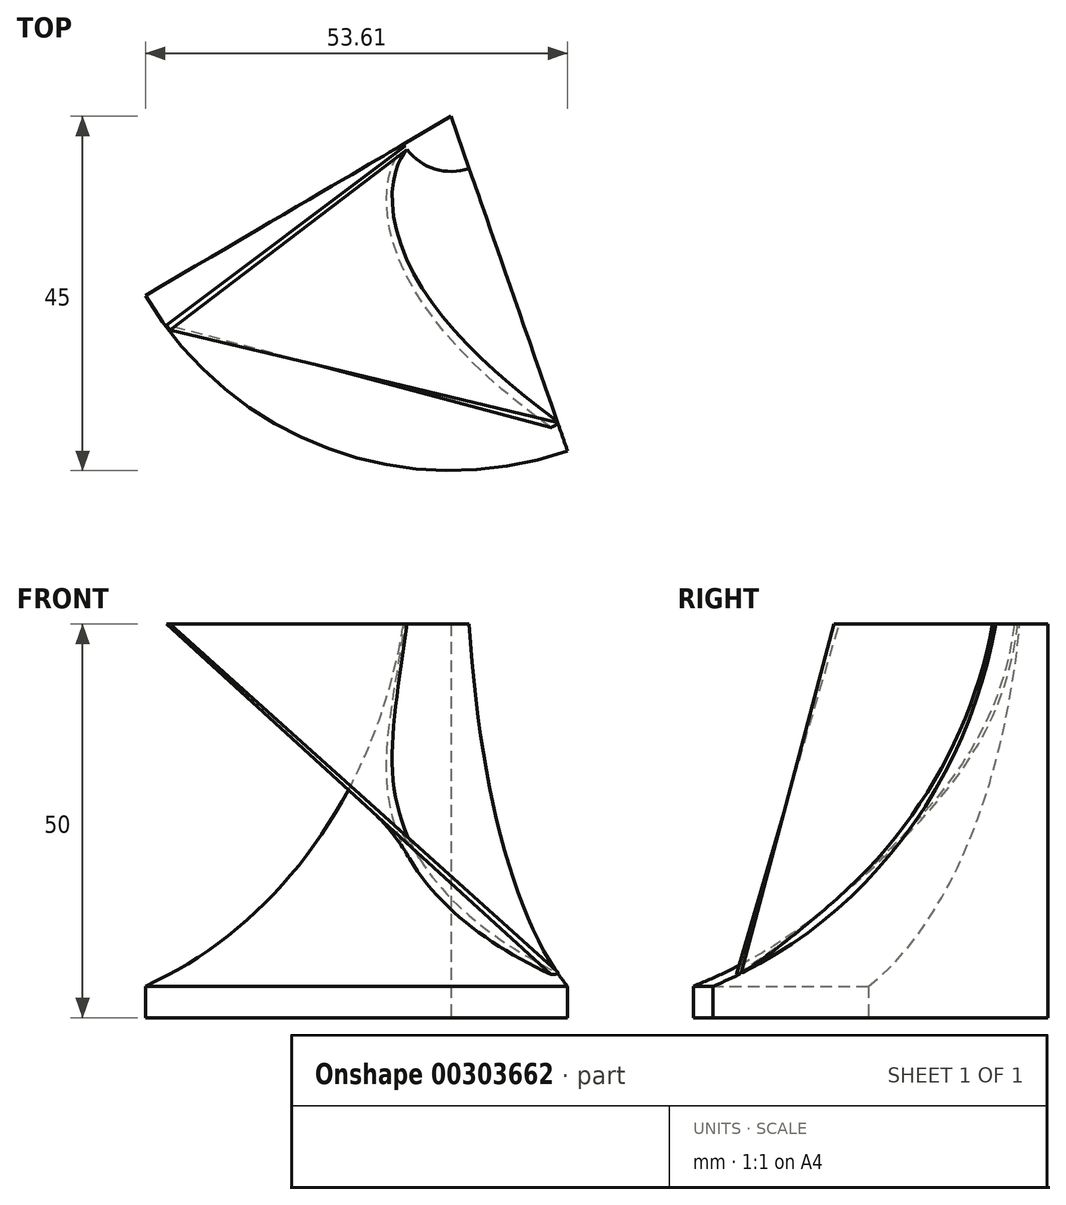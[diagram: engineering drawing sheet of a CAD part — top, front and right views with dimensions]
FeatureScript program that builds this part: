
annotation { "Feature Type Name" : "Feature", "Feature Type Description" : "" }
export const myFeature = defineFeature(function(context is Context, id is Id, definition is map)
    precondition{}
    {
        {
            var Q0;
            Q0=qCreatedBy(makeId("Front.planeOp"),FACE);
            var sketch = newSketch(context, id + "F0", { "sketchPlane" : qUnion([Q0])});
            skLineSegment(sketch, "E0", {"start": v(0, 0) * mm, "end": v(0, 50) * mm});
            skLineSegment(sketch, "E1", {"start": v(0, 0) * mm, "end": v(45, 0) * mm});
            skLineSegment(sketch, "E2", {"start": v(0, 50) * mm, "end": v(7, 50) * mm});
            skLineSegment(sketch, "E3", {"start": v(45, 0) * mm, "end": v(45, 4) * mm});
            skArc(sketch, "E4", {"start": v(7, 50) * mm, "mid": v(20.03, 22.07) * mm, "end": v(45, 4) * mm});
            skSolve(sketch);
        }
        {
            var Q0;
            Q0=makeQuery(id+"F0.imprint","IMPRINT",FACE,{"disambiguationData":[TD([[makeQuery(id+"F0.imprint","IMPRINT",EDGE,{"derivedFrom":sQuery(id+"F0.wireOp",EDGE,"E0")}),-1.0]])]});
            var Q1;
            Q1=sQuery(id+"F0.wireOp",EDGE,"E0");
            revolve(context, id + "F1", {"entities" : qUnion([Q0]), "axis" : qUnion([Q1]), "revolveType" : RevolveType.FULL});
        }
        {
            var Q0;
            Q0=makeQuery(id+"F1.opRevolve","SWEPT_FACE",FACE,{"disambiguationData":[OSD([sQuery(id+"F0.wireOp",EDGE,"E1")])]});
            cPlane(context, id + "F2", {"entities" : qUnion([Q0]), "cplaneType" : CPlaneType.OFFSET, "offset" : 0 * mm, "width" : 152.4 * mm, "height" : 152.4 * mm});
        }
        {
            var Q0;
            Q0=qCreatedBy(id+"F2.planeOp",FACE);
            var sketch = newSketch(context, id + "F3", { "sketchPlane" : qUnion([Q0])});
            skLineSegment(sketch, "E5", {"start": v(0, 0) * mm, "end": v(1.5, 0) * mm});
            skArc(sketch, "E6", {"start": v(18.7, 41.14) * mm, "mid": v(5.44, 22.35) * mm, "end": v(0, 0) * mm});
            skLineSegment(sketch, "E7", {"start": v(18.7, 41.14) * mm, "end": v(20.03, 40.45) * mm});
            skArc(sketch, "E8", {"start": v(20.03, 40.45) * mm, "mid": v(7.3, 21.81) * mm, "end": v(1.5, 0) * mm});
            skSolve(sketch);
        }
        {
            var Q0;
            Q0=makeQuery(id+"F1.opRevolve","SWEPT_FACE",FACE,{"disambiguationData":[OSD([sQuery(id+"F0.wireOp",EDGE,"E2")])]});
            var sketch = newSketch(context, id + "F4", { "sketchPlane" : qUnion([Q0])});
            skLineSegment(sketch, "E9", {"start": v(0, 0) * mm, "end": v(-0.8, 0) * mm});
            skLineSegment(sketch, "E10", {"start": v(-0.8, 0) * mm, "end": v(-36.17, -26.48) * mm});
            skLineSegment(sketch, "E11", {"start": v(-36.17, -26.48) * mm, "end": v(-35.69, -27.12) * mm});
            skLineSegment(sketch, "E12", {"start": v(-35.69, -27.12) * mm, "end": v(0, 0) * mm});
            skSolve(sketch);
        }
        {
            var Q1;
            Q1=makeQuery(id+"F3.imprint","IMPRINT",FACE,{"disambiguationData":[TD([[makeQuery(id+"F3.imprint","IMPRINT",EDGE,{"derivedFrom":sQuery(id+"F3.wireOp",EDGE,"E5")}),1.0]])]});
            var Q2;
            {var subQ0=sQuery(id+"F4.wireOp",EDGE,"E11");Q2=makeQuery(id+"F4.imprint","IMPRINT",FACE,{"disambiguationData":[TD([[makeQuery(id+"F4.imprint","IMPRINT",EDGE,{"derivedFrom":subQ0}),1.0]])]});}
            loft(context, id + "F5", {"operationType" : NewBodyOperationType.ADD, "sheetProfilesArray" : [{ "sheetProfileEntities" : qUnion([Q1]) }, { "sheetProfileEntities" : qUnion([Q2]) }]});
        }
        {
            var Q0;
            Q0=qCreatedBy(makeId("Top.planeOp"),FACE);
            var sketch = newSketch(context, id + "F6", { "sketchPlane" : qUnion([Q0])});
            skLineSegment(sketch, "E13", {"start": v(0, 0) * mm, "end": v(-48.77, -28.58) * mm});
            skLineSegment(sketch, "E14", {"start": v(-48.77, -28.58) * mm, "end": v(-48.77, 43.52) * mm});
            skLineSegment(sketch, "E15", {"start": v(-48.77, 43.52) * mm, "end": v(31.93, 47.7) * mm});
            skLineSegment(sketch, "E16", {"start": v(31.93, 47.7) * mm, "end": v(58.23, 43.52) * mm});
            skLineSegment(sketch, "E17", {"start": v(58.23, 43.52) * mm, "end": v(50.1, -75.3) * mm});
            skLineSegment(sketch, "E18", {"start": v(50.1, -75.3) * mm, "end": v(24.19, -69.5) * mm});
            skLineSegment(sketch, "E19", {"start": v(24.19, -69.5) * mm, "end": v(0, 0) * mm});
            skSolve(sketch);
        }
        {
            var Q0;
            Q0=makeQuery(id+"F6.imprint","IMPRINT",FACE,{"disambiguationData":[TD([[makeQuery(id+"F6.imprint","IMPRINT",EDGE,{"derivedFrom":sQuery(id+"F6.wireOp",EDGE,"E13")}),-1.0]])]});
            extrude(context, id + "F7", {"entities" : qUnion([Q0]), "operationType" : NewBodyOperationType.REMOVE, "depth" : 66.3 * mm});
        }
    });
